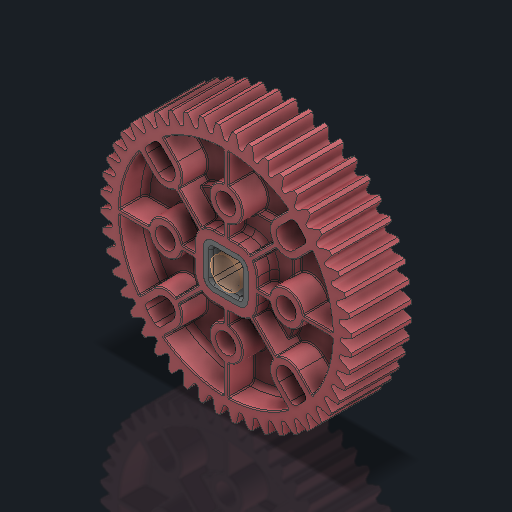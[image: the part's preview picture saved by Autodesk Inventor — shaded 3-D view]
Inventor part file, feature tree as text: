
AUTODESK INVENTOR PART (.ipt)
format: ipt  version: 2023.2 (Build 272271030, 271C)  size: 4,134,912 bytes
history: native  units: in
note: dims shown in document units (in); Inventor stores cm internally (conversion verified against a paired STEP export)
features: other x6, sketch x1
ambient origin geometry x8: Origin, YZ Plane, XZ Plane, XY Plane, X Axis, Y Axis, Z Axis, Center Point
bodies: Solid1 (feature_tree), Solid2 (feature_tree)
feature tree (7):
  other  "HS 48T Gear, No Insert.ipt"
  other  "Solid1::HS 48T Gear, No Insert.ipt"
  other  "Solid2::HS 48T Gear, No Insert.ipt"
  other  "TaggingFeature1"
  sketch  "Sketch1"  dims[d0=0.3937in]
  other  "Srf1"
  other  "Srf1::Derived"
